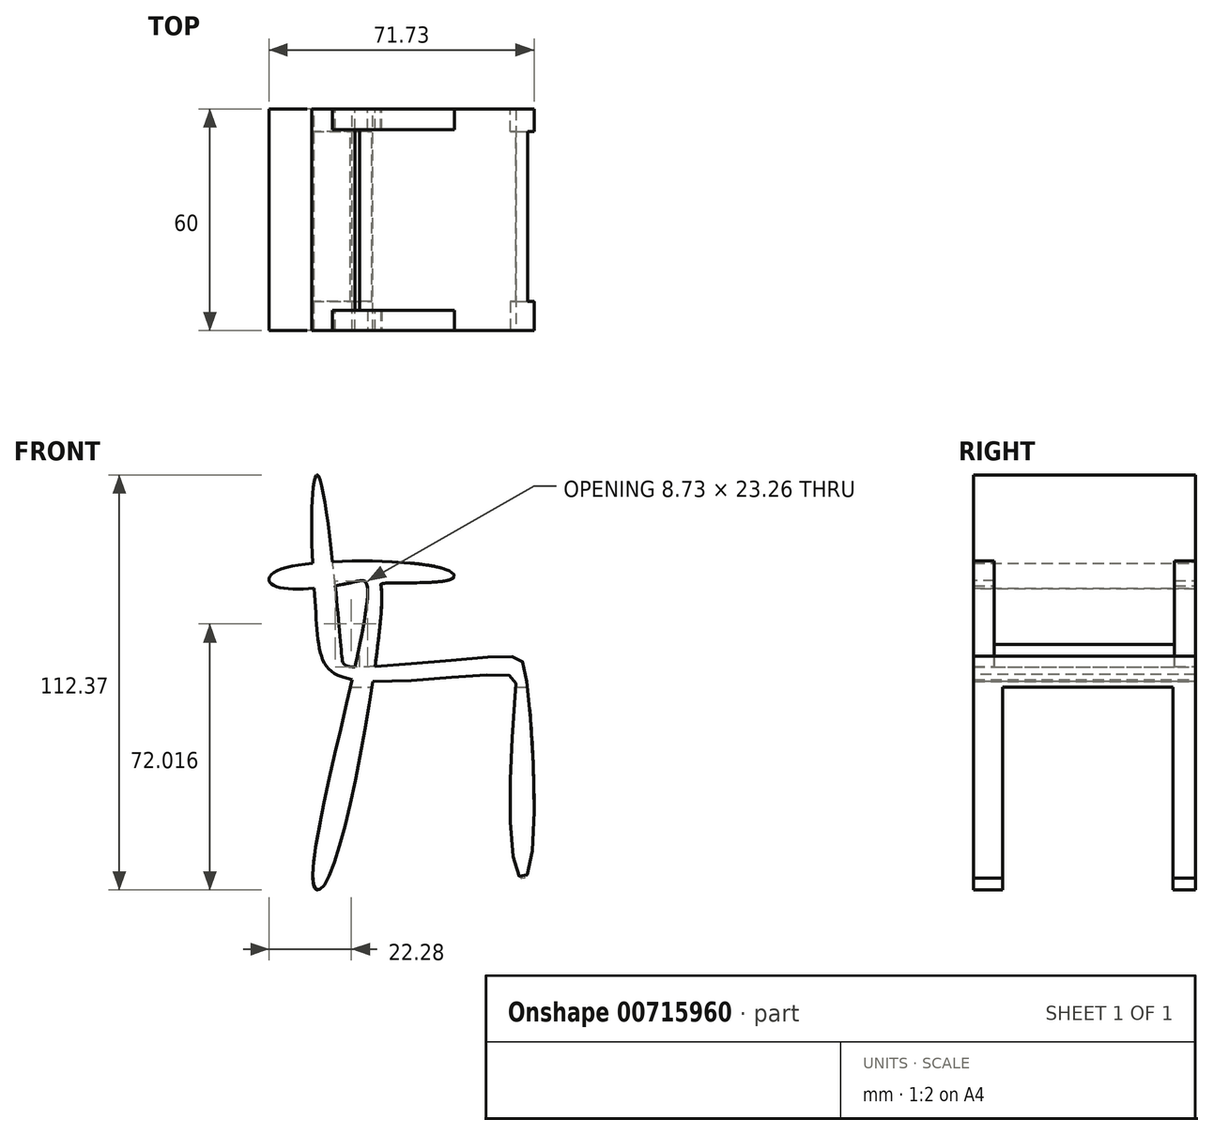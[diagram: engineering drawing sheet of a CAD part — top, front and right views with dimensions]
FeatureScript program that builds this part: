
annotation { "Feature Type Name" : "Feature", "Feature Type Description" : "" }
export const myFeature = defineFeature(function(context is Context, id is Id, definition is map)
    precondition{}
    {
        {
            var Q0;
            Q0=qCreatedBy(makeId("Front.planeOp"),FACE);
            var sketch = newSketch(context, id + "F0", { "sketchPlane" : qUnion([Q0])});
            skFitSpline(sketch, "E0", {"points": [v(-52.95, 60.95) * mm, v(-51.88, 24.26) * mm, v(-44.37, 10.32) * mm, v(0, 10.96) * mm, v(1.75, 5.39) * mm, v(2.4, -42.67) * mm, v(4.97, -43.1) * mm, v(4.54, 12.04) * mm, v(0, 16.11) * mm, v(-42.66, 13.32) * mm, v(-45.23, 17.4) * mm, v(-51.45, 65.03) * mm, v(-52.95, 60.95) * mm]});
            skSolve(sketch);
        }
        {
            var Q0;
            Q0 = qSketchRegion(id + "F0", true);
            extrude(context, id + "F1", {"entities" : qUnion([Q0]), "depth" : 60 * mm, "offsetDistance" : 25.4 * mm});
        }
        {
            var Q0;
            Q0=qCreatedBy(makeId("Front.planeOp"),FACE);
            var sketch = newSketch(context, id + "F2", { "sketchPlane" : qUnion([Q0])});
            skFitSpline(sketch, "E1", {"points": [v(-63.5, 38.83) * mm, v(-16.52, 39.47) * mm, v(-15.23, 37.11) * mm, v(-34.11, 35.83) * mm, v(-34.33, 33.9) * mm, v(-49.99, -45.91) * mm, v(-52.78, -45.7) * mm, v(-38.19, 34.97) * mm, v(-42.7, 36.04) * mm, v(-63.72, 35.4) * mm, v(-63.5, 38.83) * mm]});
            skSolve(sketch);
        }
        {
            var Q0;
            Q0 = qSketchRegion(id + "F2", true);
            extrude(context, id + "F3", {"entities" : qUnion([Q0]), "operationType" : NewBodyOperationType.ADD, "depth" : 60 * mm, "offsetDistance" : 25 * mm});
        }
        {
            var Q0;
            Q0=qCreatedBy(makeId("Right.planeOp"),FACE);
            var sketch = newSketch(context, id + "F4", { "sketchPlane" : qUnion([Q0])});
            skLineSegment(sketch, "E2.bottom", {"start": v(-52.1, 7.8) * mm, "end": v(-6.1, 7.8) * mm});
            skLineSegment(sketch, "E2.top", {"start": v(-52.1, -50.2) * mm, "end": v(-6.1, -50.2) * mm});
            skLineSegment(sketch, "E2.left", {"start": v(-52.1, 7.8) * mm, "end": v(-52.1, -50.2) * mm});
            skLineSegment(sketch, "E2.right", {"start": v(-6.1, 7.8) * mm, "end": v(-6.1, -50.2) * mm});
            skSolve(sketch);
        }
        {
            var Q0;
            Q0 = qSketchRegion(id + "F4", true);
            extrude(context, id + "F5", {"entities" : qUnion([Q0]), "operationType" : NewBodyOperationType.REMOVE, "oppositeDirection" : true, "depth" : 62.9 * mm, "offsetDistance" : 25 * mm, "hasSecondDirection" : true, "secondDirectionOppositeDirection" : false, "secondDirectionDepth" : 25 * mm});
        }
        {
            var Q0;
            Q0=qCreatedBy(makeId("Right.planeOp"),FACE);
            var sketch = newSketch(context, id + "F6", { "sketchPlane" : qUnion([Q0])});
            skLineSegment(sketch, "E3.bottom", {"start": v(-54.41, 59.38) * mm, "end": v(-5.64, 59.38) * mm});
            skLineSegment(sketch, "E3.top", {"start": v(-54.41, 19.29) * mm, "end": v(-5.64, 19.29) * mm});
            skLineSegment(sketch, "E3.left", {"start": v(-54.41, 59.38) * mm, "end": v(-54.41, 19.29) * mm});
            skLineSegment(sketch, "E3.right", {"start": v(-5.64, 59.38) * mm, "end": v(-5.64, 19.29) * mm});
            skSolve(sketch);
        }
        {
            var Q0;
            Q0 = qSketchRegion(id + "F6", true);
            var Q1;
            Q1=makeQuery(id+"F3.boolean.opBoolean","SPLIT",FACE,{"disambiguationData":[OD(2.0)],"derivedFrom":makeQuery(id+"F1.opExtrude","SWEPT_FACE",FACE,{"disambiguationData":[OSD([sQuery(id+"F0.wireOp",EDGE,"E0")])]})});
            var Q2;
            Q2=makeQuery(id+"F3.boolean.opBoolean","SPLIT",FACE,{"disambiguationData":[OD(2.0)],"derivedFrom":makeQuery(id+"F1.opExtrude","SWEPT_FACE",FACE,{"disambiguationData":[OSD([sQuery(id+"F0.wireOp",EDGE,"E0")])]})});
            extrude(context, id + "F7", {"entities" : qUnion([Q0]), "operationType" : NewBodyOperationType.REMOVE, "endBound" : BoundingType.UP_TO_SURFACE, "oppositeDirection" : true, "depth" : 49.8 * mm, "endBoundEntityFace" : qUnion([Q1]), "offsetDistance" : 25 * mm});
        }
        {
            var Q0;
            Q0=qCreatedBy(makeId("Top.planeOp"),FACE);
            cPlane(context, id + "F8", {"entities" : qUnion([Q0]), "cplaneType" : CPlaneType.OFFSET, "offset" : 14.1 * mm, "width" : 150 * mm, "height" : 150 * mm});
        }
        {
            var Q0;
            Q0=qCreatedBy(id+"F8.planeOp",FACE);
            var sketch = newSketch(context, id + "F9", { "sketchPlane" : qUnion([Q0])});
            skLineSegment(sketch, "E4.bottom", {"start": v(-39.9, -6.15) * mm, "end": v(-35.2, -6.15) * mm});
            skLineSegment(sketch, "E4.top", {"start": v(-39.9, -54.2) * mm, "end": v(-35.2, -54.2) * mm});
            skLineSegment(sketch, "E4.left", {"start": v(-39.9, -6.15) * mm, "end": v(-39.9, -54.2) * mm});
            skLineSegment(sketch, "E4.right", {"start": v(-35.2, -6.15) * mm, "end": v(-35.2, -54.2) * mm});
            skSolve(sketch);
        }
        {
            var Q0;
            Q0 = qSketchRegion(id + "F9", true);
            var Q1;
            Q1=makeQuery(id+"F7.boolean.opBoolean","COPY",FACE,{"derivedFrom":makeQuery(id+"F7.opExtrude","SWEPT_FACE",FACE,{"disambiguationData":[OSD([sQuery(id+"F6.wireOp",EDGE,"E3.top")])]})});
            var Q2;
            Q2=makeQuery(id+"F3.boolean.opBoolean","SPLIT",FACE,{"disambiguationData":[OD(3.0)],"derivedFrom":makeQuery(id+"F1.opExtrude","SWEPT_FACE",FACE,{"disambiguationData":[OSD([sQuery(id+"F0.wireOp",EDGE,"E0")])]})});
            extrude(context, id + "F10", {"entities" : qUnion([Q0, Q1]), "operationType" : NewBodyOperationType.REMOVE, "endBound" : BoundingType.UP_TO_SURFACE, "oppositeDirection" : true, "depth" : 25 * mm, "endBoundEntityFace" : qUnion([Q2]), "offsetDistance" : 25 * mm});
        }
    });
